# Revit family: Door_Sliding_BiPart_Tormax_TX9600-ICU-Surface
name_source: partatom
category: Doors
units: mm (PartAtom-declared; Revit-internal decimal feet)

## family parameters
Always vertical = Yes
Classification Number = 23.30.10.17.11
Cut with Voids When Loaded = No
Host = Wall
Room Calculation Point = No
Shared = No

## types (3) — shared parameters
Air Infiltration = as Specified
Analytic Construction = <None>
Assembly Code = B2030110
Available Options = as Specified
Breakout_Partial = Yes
Center Rail Width = 0' - 1 3/4"
Construction Details = http://www.arcat.com
Define Thermal Properties by = Schematic Type
Description = Tormax Surface Mounted BiPart Manual Sliding ICU Door - TX9600 as Specified
Fire Rating = as Specified
Frame Thickness = 0' - 4 1/2"
Function = Exterior
Glazing Stop Width = 0' - 0 1/4"
Green Building-LEED = http://www.arcat.com
Heat Transfer Coefficient (U) = 0.1 BTU/(h·ft²·°F)
Include Transom = No
Keynote = 08463
Manufacturer = TORMAX USA Inc.
Manufacturer Fax = 210-494-5930
Manufacturer Website = http://www.tormaxusa.com
Maximum Size = Width and Height as Specified
Miami Dade Conformance = as Specified
Model = TX9600 BiPart Surface
Operating Temperature Range = as Specified
Panel Thickness = 0' - 1 3/4"
Product Data = http://www.arcat.com
R = 0.0000 (h·ft²·°F)/BTU
RO Spacing_Sides = 0' - 0"
RO Spacing_Top = 0' - 0 1/4"
Sales Information = http://www.tormaxusa.com
Send Message = http://www.arcat.com
Smoke Rated = No
Specification = http://www.arcat.com
Standards Conformance = as Specified
Structural Test Pressure = as Specified
Thermal Resistance (R) = 0.0000 (h·ft²·°F)/BTU
Thickness = 0' - 1 3/4"
U = 0.1 BTU/(h·ft²·°F)
URL = http://www.tormaxusa.com
Wall Closure = By host
Water Penetration = as Specified
zero-valued in all types: Expected Lifespan (Years), Maintenance Schedule (Months), SHGC, Solar Heat Gain Coefficient, VLT, Visual Light Transmittance, Warranty Duration (Years)

## per-type parameters (varying)
| type | Breakout Width | Clear Door Opening Width | Panel A Width | Width |
| 10ft | 4' - 8" | 4' - 6" | 2' - 6 3/8" | 10' - 0" |
| 12ft | 5' - 8" | 5' - 6" | 3' - 0 3/8" | 11' - 0" |
| 14ft | 6' - 8" | 6' - 6" | 3' - 6 3/8" | 12' - 0" |

## geometry (parser evidence)
native form markers: Blend x2, Sweep x6
no freeform markers — native parametric forms only
